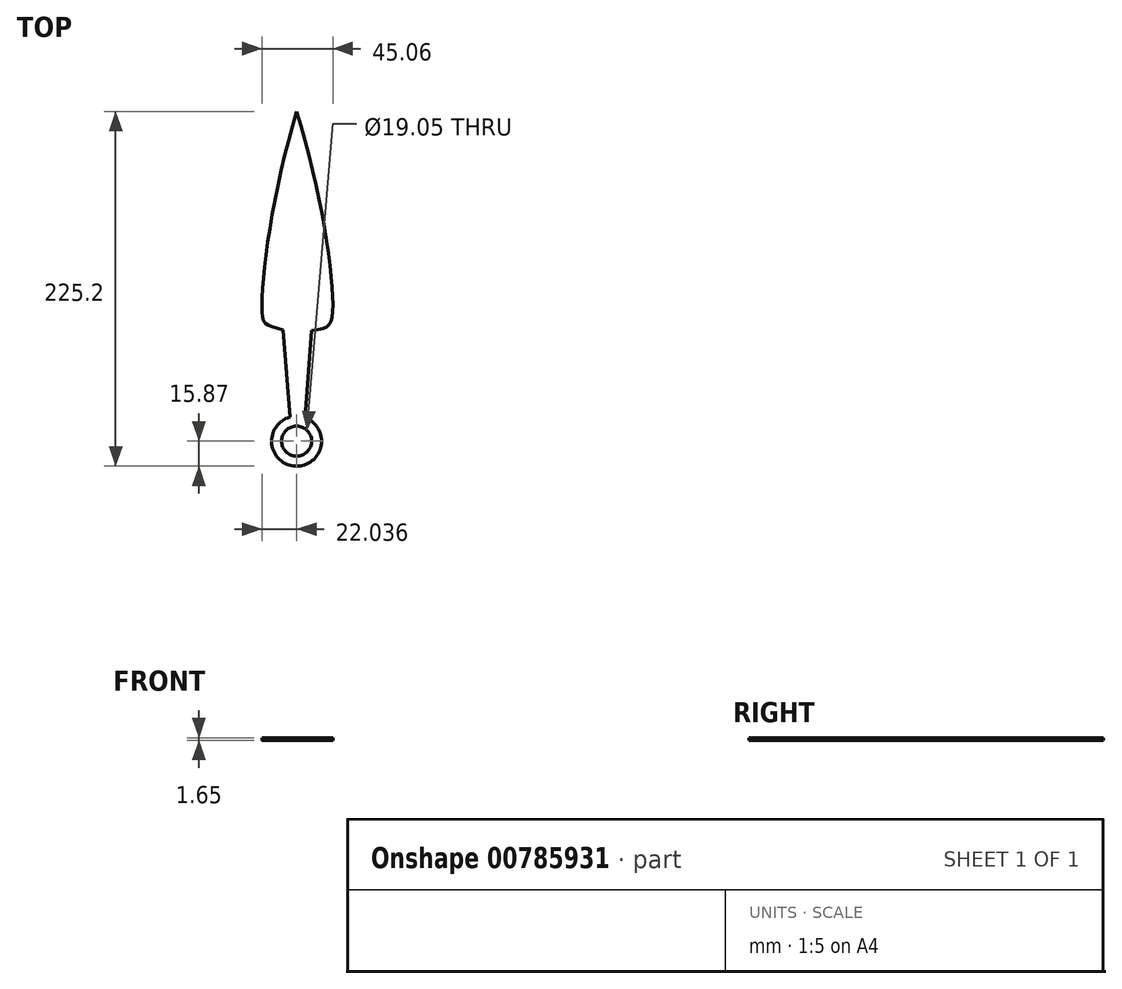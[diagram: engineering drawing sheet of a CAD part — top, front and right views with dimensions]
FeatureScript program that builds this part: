
annotation { "Feature Type Name" : "Feature", "Feature Type Description" : "" }
export const myFeature = defineFeature(function(context is Context, id is Id, definition is map)
    precondition{}
    {
        {
            var Q0;
            Q0=qCreatedBy(makeId("Top.planeOp"),FACE);
            var sketch = newSketch(context, id + "F0", { "sketchPlane" : qUnion([Q0])});
            skLineSegment(sketch, "E0.bottom", {"start": v(-55.27, -39.18) * mm, "end": v(-4.47, -39.18) * mm});
            skLineSegment(sketch, "E0.top", {"start": v(-55.27, 189.42) * mm, "end": v(-4.47, 189.42) * mm});
            skLineSegment(sketch, "E0.left", {"start": v(-55.27, -39.18) * mm, "end": v(-55.27, 189.42) * mm});
            skLineSegment(sketch, "E0.right", {"start": v(-4.47, -39.18) * mm, "end": v(-4.47, 189.42) * mm});
            skSolve(sketch);
        }
        {
            var Q0;
            Q0=makeQuery(id+"F0.imprint","IMPRINT",FACE,{"disambiguationData":[TD([[makeQuery(id+"F0.imprint","IMPRINT",EDGE,{"derivedFrom":sQuery(id+"F0.wireOp",EDGE,"E0.bottom")}),1.0]])]});
            var sketch = newSketch(context, id + "F1", { "sketchPlane" : qUnion([Q0])});
            skArc(sketch, "E1", {"start": v(-34.52, -4.84) * mm, "mid": v(-30.8, -36) * mm, "end": v(-25, -5.15) * mm});
            skLineSegment(sketch, "E2", {"start": v(-34.52, -4.84) * mm, "end": v(-38.9, 50.55) * mm});
            skLineSegment(sketch, "E3", {"start": v(-25, -5.15) * mm, "end": v(-20.64, 50.24) * mm});
            skFitSpline(sketch, "E4", {"points": [v(-38.9, 50.55) * mm, v(-51.6, 57.87) * mm, v(-30.26, 189.2) * mm], "startDerivative": vector(-110.2, 34.54) * mm, "endDerivative": vector(63.59, 209.52) * mm});
            skFitSpline(sketch, "E5", {"points": [v(-20.64, 50.24) * mm, v(-7.94, 57.87) * mm, v(-30.26, 189.2) * mm], "startDerivative": vector(107.34, 14.8) * mm, "endDerivative": vector(-64.76, 209.78) * mm});
            skCircle(sketch, "E6", {"center": v(-30.26, -20.13) * mm, "radius": 9.52 * mm});
            skSolve(sketch);
        }
        {
            var Q0;
            Q0 = qSketchRegion(id + "F1", true);
            extrude(context, id + "F2", {"entities" : qUnion([Q0]), "depth" : 1.65 * mm, "offsetDistance" : 25.4 * mm});
        }
    });
